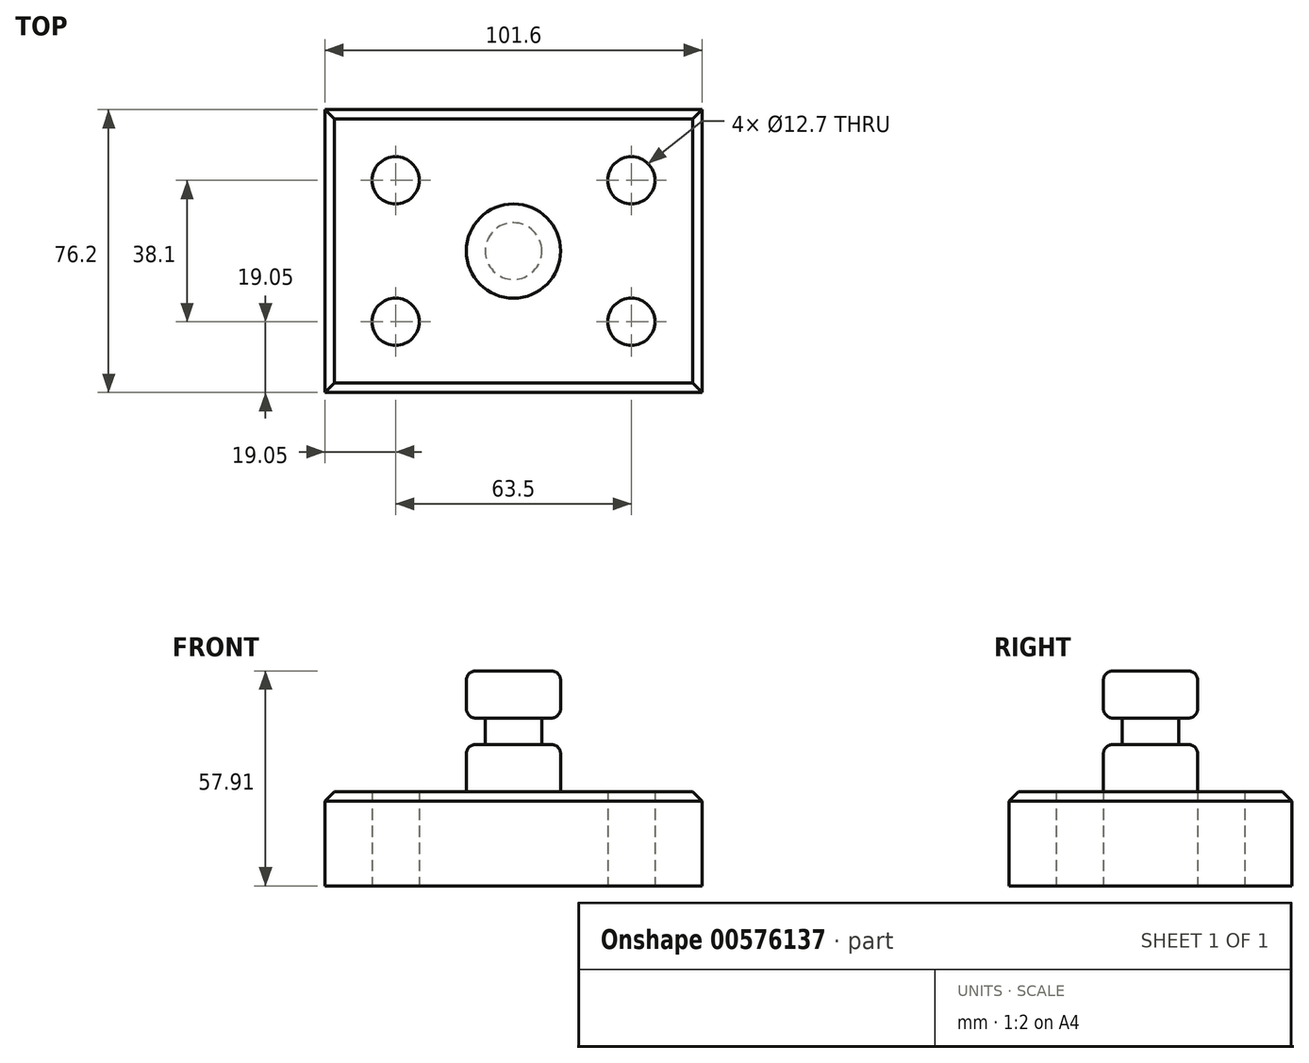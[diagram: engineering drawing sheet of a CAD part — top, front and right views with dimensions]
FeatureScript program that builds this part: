
annotation { "Feature Type Name" : "Feature", "Feature Type Description" : "" }
export const myFeature = defineFeature(function(context is Context, id is Id, definition is map)
    precondition{}
    {
        {
            var Q0;
            Q0=qCreatedBy(makeId("Top.planeOp"),FACE);
            var sketch = newSketch(context, id + "F0", { "sketchPlane" : qUnion([Q0])});
            skLineSegment(sketch, "E0.bottom", {"start": v(-50.8, 38.1) * mm, "end": v(50.8, 38.1) * mm});
            skLineSegment(sketch, "E0.top", {"start": v(-50.8, -38.1) * mm, "end": v(50.8, -38.1) * mm});
            skLineSegment(sketch, "E0.left", {"start": v(-50.8, 38.1) * mm, "end": v(-50.8, -38.1) * mm});
            skLineSegment(sketch, "E0.right", {"start": v(50.8, 38.1) * mm, "end": v(50.8, -38.1) * mm});
            skPoint(sketch, "E0.middle", {"position": v(0, 0) * mm});
            skSolve(sketch);
        }
        {
            var Q0;
            Q0=makeQuery(id+"F0.imprint","IMPRINT",FACE,{"disambiguationData":[TD([[makeQuery(id+"F0.imprint","IMPRINT",EDGE,{"derivedFrom":sQuery(id+"F0.wireOp",EDGE,"E0.bottom")}),-1.0]])]});
            extrude(context, id + "F1", {"entities" : qUnion([Q0]), "depth" : 25.4 * mm, "offsetDistance" : 25.4 * mm});
        }
        {
            var Q0;
            Q0=makeQuery(id+"F1.opExtrude","CAP_FACE",FACE,{"disambiguationData":[OSD([sQuery(id+"F0.wireOp",EDGE,"E0.bottom"),sQuery(id+"F0.wireOp",EDGE,"E0.top"),sQuery(id+"F0.wireOp",EDGE,"E0.left"),sQuery(id+"F0.wireOp",EDGE,"E0.right")])],"isStart":true});
            var sketch = newSketch(context, id + "F2", { "sketchPlane" : qUnion([Q0])});
            skCircle(sketch, "E1", {"center": v(31.75, 19.05) * mm, "radius": 6.35 * mm});
            skCircle(sketch, "E2", {"center": v(31.75, -19.05) * mm, "radius": 6.35 * mm});
            skCircle(sketch, "E3", {"center": v(-31.75, 19.05) * mm, "radius": 6.35 * mm});
            skCircle(sketch, "E4", {"center": v(-31.75, -19.05) * mm, "radius": 6.35 * mm});
            skSolve(sketch);
        }
        {
            var Q0;
            Q0=makeQuery(id+"F2.imprint","IMPRINT",FACE,{"disambiguationData":[TD([[makeQuery(id+"F2.imprint","IMPRINT",EDGE,{"derivedFrom":sQuery(id+"F2.wireOp",EDGE,"E1")}),1.0]])]});
            var Q1;
            Q1=makeQuery(id+"F2.imprint","IMPRINT",FACE,{"disambiguationData":[TD([[makeQuery(id+"F2.imprint","IMPRINT",EDGE,{"derivedFrom":sQuery(id+"F2.wireOp",EDGE,"E2")}),1.0]])]});
            var Q2;
            Q2=makeQuery(id+"F2.imprint","IMPRINT",FACE,{"disambiguationData":[TD([[makeQuery(id+"F2.imprint","IMPRINT",EDGE,{"derivedFrom":sQuery(id+"F2.wireOp",EDGE,"E4")}),1.0]])]});
            var Q3;
            Q3=makeQuery(id+"F2.imprint","IMPRINT",FACE,{"disambiguationData":[TD([[makeQuery(id+"F2.imprint","IMPRINT",EDGE,{"derivedFrom":sQuery(id+"F2.wireOp",EDGE,"E3")}),1.0]])]});
            extrude(context, id + "F3", {"entities" : qUnion([Q0, Q1, Q2, Q3]), "operationType" : NewBodyOperationType.REMOVE, "endBound" : BoundingType.THROUGH_ALL, "oppositeDirection" : true, "depth" : 25.4 * mm, "offsetDistance" : 25.4 * mm});
        }
        {
            var Q0;
            Q0=qCreatedBy(makeId("Front.planeOp"),FACE);
            var sketch = newSketch(context, id + "F4", { "sketchPlane" : qUnion([Q0])});
            skLineSegment(sketch, "E5.bottom", {"start": v(0, 25.4) * mm, "end": v(12.7, 25.4) * mm});
            skLineSegment(sketch, "E5.top", {"start": v(0, 38.1) * mm, "end": v(12.7, 38.1) * mm});
            skLineSegment(sketch, "E5.left", {"start": v(0, 25.4) * mm, "end": v(0, 38.1) * mm});
            skLineSegment(sketch, "E5.right", {"start": v(12.7, 25.4) * mm, "end": v(12.7, 38.1) * mm});
            skSolve(sketch);
        }
        {
            var Q0;
            Q0 = qSketchRegion(id + "F4", true);
            var Q1;
            Q1=sQuery(id+"F4.wireOp",EDGE,"E5.left");
            revolve(context, id + "F5", {"operationType" : NewBodyOperationType.ADD, "entities" : qUnion([Q0]), "axis" : qUnion([Q1]), "revolveType" : RevolveType.FULL});
        }
        {
            var Q0;
            Q0=qCreatedBy(makeId("Front.planeOp"),FACE);
            var sketch = newSketch(context, id + "F6", { "sketchPlane" : qUnion([Q0])});
            skLineSegment(sketch, "E6.bottom", {"start": v(0, 38.1) * mm, "end": v(7.62, 38.1) * mm});
            skLineSegment(sketch, "E6.top", {"start": v(0, 45.21) * mm, "end": v(7.62, 45.21) * mm});
            skLineSegment(sketch, "E6.left", {"start": v(0, 38.1) * mm, "end": v(0, 45.21) * mm});
            skLineSegment(sketch, "E6.right", {"start": v(7.62, 38.1) * mm, "end": v(7.62, 45.21) * mm});
            skSolve(sketch);
        }
        {
            var Q0;
            Q0 = qSketchRegion(id + "F6", true);
            var Q1;
            Q1=sQuery(id+"F6.wireOp",EDGE,"E6.left");
            revolve(context, id + "F7", {"operationType" : NewBodyOperationType.ADD, "entities" : qUnion([Q0]), "axis" : qUnion([Q1]), "revolveType" : RevolveType.FULL});
        }
        {
            var Q0;
            Q0=qCreatedBy(makeId("Front.planeOp"),FACE);
            var sketch = newSketch(context, id + "F8", { "sketchPlane" : qUnion([Q0])});
            skLineSegment(sketch, "E7.bottom", {"start": v(0, 57.91) * mm, "end": v(-12.7, 57.91) * mm});
            skLineSegment(sketch, "E7.top", {"start": v(0, 45.21) * mm, "end": v(-12.7, 45.21) * mm});
            skLineSegment(sketch, "E7.left", {"start": v(0, 57.91) * mm, "end": v(0, 45.21) * mm});
            skLineSegment(sketch, "E7.right", {"start": v(-12.7, 57.91) * mm, "end": v(-12.7, 45.21) * mm});
            skSolve(sketch);
        }
        {
            var Q0;
            Q0=makeQuery(id+"F8.imprint","IMPRINT",FACE,{"disambiguationData":[TD([[makeQuery(id+"F8.imprint","IMPRINT",EDGE,{"derivedFrom":sQuery(id+"F8.wireOp",EDGE,"E7.bottom")}),1.0]])]});
            var Q1;
            Q1=sQuery(id+"F8.wireOp",EDGE,"E7.left");
            revolve(context, id + "F9", {"operationType" : NewBodyOperationType.ADD, "entities" : qUnion([Q0]), "axis" : qUnion([Q1]), "revolveType" : RevolveType.FULL});
        }
        {
            var Q0;
            Q0=makeQuery(id+"F9.opRevolve","SWEPT_EDGE",EDGE,{"disambiguationData":[OSD([sQuery(id+"F8.wireOp",EDGE,"E7.bottom"),sQuery(id+"F8.wireOp",EDGE,"E7.right")])]});
            fillet(context, id + "F10", {"entities" : qUnion([Q0]), "radius" : 2.54 * mm, "tangentPropagation" : true, "allowEdgeOverflow" : false});
        }
        {
            var Q0;
            Q0=makeQuery(id+"F1.opExtrude","CAP_EDGE",EDGE,{"disambiguationData":[OSD([sQuery(id+"F0.wireOp",EDGE,"E0.top")])],"isStart":false});
            var Q1;
            Q1=makeQuery(id+"F1.opExtrude","CAP_EDGE",EDGE,{"disambiguationData":[OSD([sQuery(id+"F0.wireOp",EDGE,"E0.left")])],"isStart":false});
            var Q2;
            Q2=makeQuery(id+"F1.opExtrude","CAP_EDGE",EDGE,{"disambiguationData":[OSD([sQuery(id+"F0.wireOp",EDGE,"E0.bottom")])],"isStart":false});
            var Q3;
            Q3=makeQuery(id+"F1.opExtrude","CAP_EDGE",EDGE,{"disambiguationData":[OSD([sQuery(id+"F0.wireOp",EDGE,"E0.right")])],"isStart":false});
            chamfer(context, id + "F11", {"entities" : qUnion([Q0, Q1, Q2, Q3]), "width" : 2.54 * mm, "tangentPropagation" : true});
        }
        {
            var Q0;
            Q0=makeQuery(id+"F5.opRevolve","SWEPT_EDGE",EDGE,{"disambiguationData":[OSD([sQuery(id+"F4.wireOp",EDGE,"E5.bottom"),sQuery(id+"F4.wireOp",EDGE,"E5.right")])]});
            var Q1;
            Q1=makeQuery(id+"F5.opRevolve","SWEPT_EDGE",EDGE,{"disambiguationData":[OSD([sQuery(id+"F4.wireOp",EDGE,"E5.top"),sQuery(id+"F4.wireOp",EDGE,"E5.right")])]});
            var Q2;
            Q2=makeQuery(id+"F9.opRevolve","SWEPT_EDGE",EDGE,{"disambiguationData":[OSD([sQuery(id+"F8.wireOp",EDGE,"E7.top"),sQuery(id+"F8.wireOp",EDGE,"E7.right")])]});
            fillet(context, id + "F12", {"entities" : qUnion([Q0, Q1, Q2]), "radius" : 2.54 * mm, "tangentPropagation" : true, "allowEdgeOverflow" : false});
        }
    });
